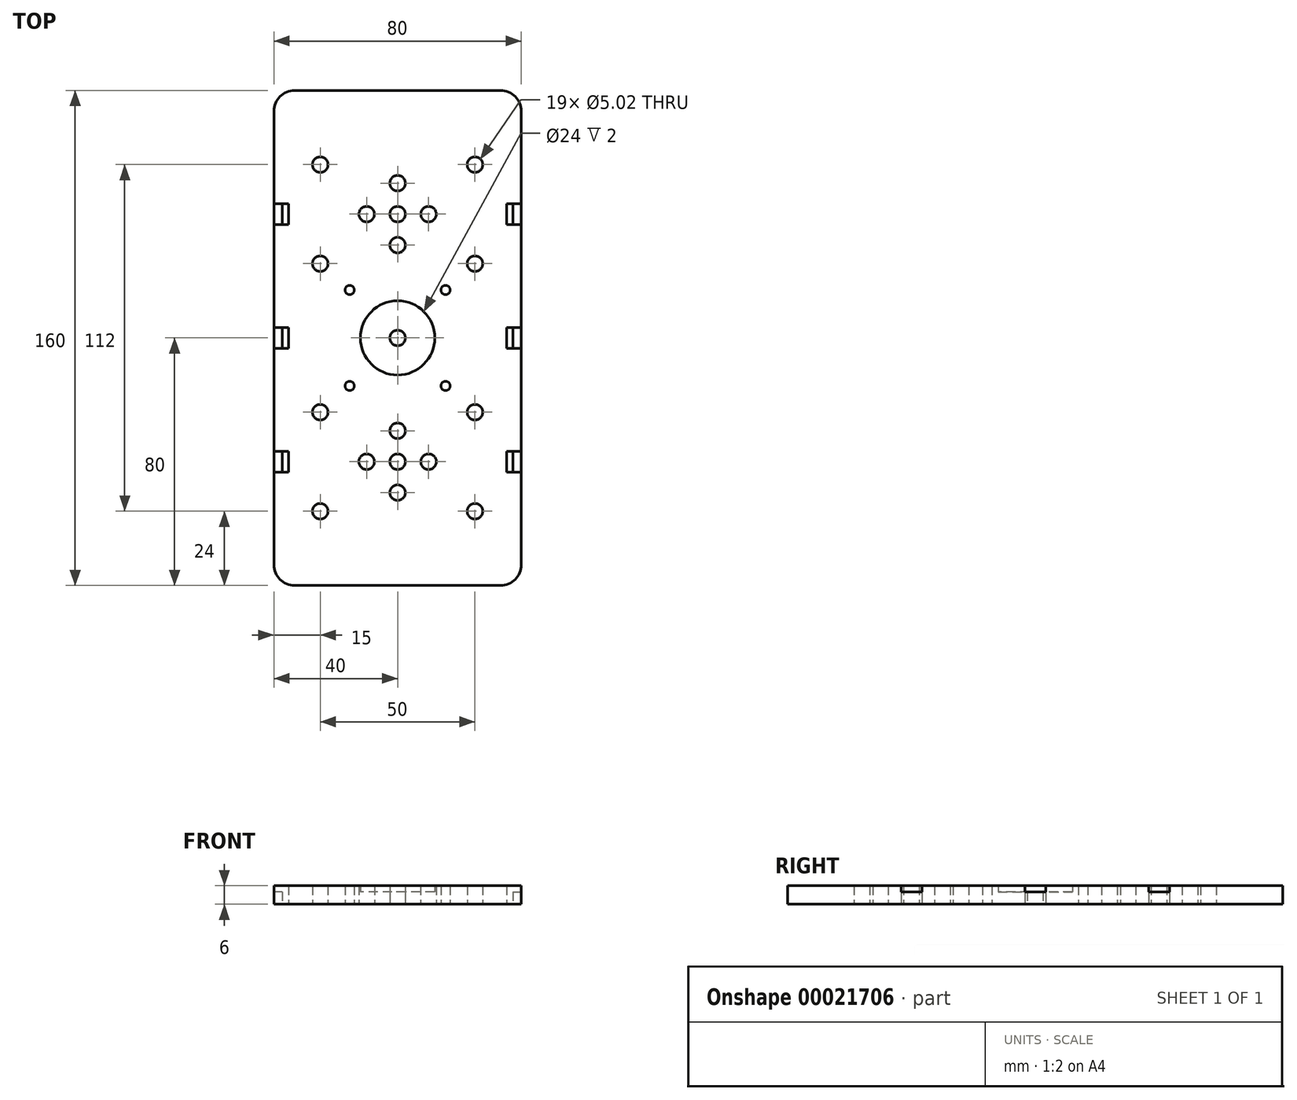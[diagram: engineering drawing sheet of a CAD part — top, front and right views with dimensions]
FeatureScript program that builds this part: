
annotation { "Feature Type Name" : "Feature", "Feature Type Description" : "" }
export const myFeature = defineFeature(function(context is Context, id is Id, definition is map)
    precondition{}
    {
        {
            var Q0;
            Q0=qCreatedBy(makeId("Top.planeOp"),FACE);
            var sketch = newSketch(context, id + "F2", { "sketchPlane" : qUnion([Q0])});
            skLineSegment(sketch, "E0", {"start": v(0, 0) * mm, "end": v(0, 40) * mm, "construction": true});
            skLineSegment(sketch, "E1", {"start": v(0, 0) * mm, "end": v(40, 0) * mm, "construction": true});
            skLineSegment(sketch, "E2", {"start": v(40, 0) * mm, "end": v(40, 33.3) * mm});
            skLineSegment(sketch, "E3", {"start": v(33.3, 40) * mm, "end": v(0, 40) * mm});
            skCircle(sketch, "E4", {"center": v(0, 0) * mm, "radius": 2.5 * mm, "construction": true});
            skLineSegment(sketch, "E5", {"start": v(25, 0) * mm, "end": v(25, 16) * mm, "construction": true});
            skLineSegment(sketch, "E6", {"start": v(25, 16) * mm, "end": v(0, 16) * mm, "construction": true});
            skCircle(sketch, "E7", {"center": v(25, 16) * mm, "radius": 2.5 * mm});
            skPoint(sketch, "E8.visualSharp", {"position": v(40, 40) * mm});
            skArc(sketch, "E8.filletArc", {"start": v(40, 33.3) * mm, "mid": v(38.04, 38.04) * mm, "end": v(33.3, 40) * mm});
            skLineSegment(sketch, "E9", {"start": v(37.26, 0) * mm, "end": v(37.26, 3.35) * mm});
            skLineSegment(sketch, "E10", {"start": v(37.26, 3.35) * mm, "end": v(40, 3.35) * mm});
            skLineSegment(sketch, "E11", {"start": v(37.26, 3.35) * mm, "end": v(35.26, 3.35) * mm});
            skLineSegment(sketch, "E12", {"start": v(35.26, 3.35) * mm, "end": v(35.26, 0) * mm});
            skCircle(sketch, "E13", {"center": v(10, 0) * mm, "radius": 2.5 * mm, "construction": true});
            skCircle(sketch, "E14", {"center": v(0, 10) * mm, "radius": 2.5 * mm, "construction": true});
            skLineSegment(sketch, "E15", {"start": v(10, 0) * mm, "end": v(0, 0) * mm, "construction": true});
            skLineSegment(sketch, "E16", {"start": v(0, 10) * mm, "end": v(0, 0) * mm, "construction": true});
            skArc(sketch, "E17", {"start": v(2.5, 0) * mm, "mid": v(1.77, 1.77) * mm, "end": v(0, 2.5) * mm});
            skArc(sketch, "E18", {"start": v(12.5, 0) * mm, "mid": v(10, 2.51) * mm, "end": v(7.5, 0) * mm});
            skArc(sketch, "E19", {"start": v(0, 7.5) * mm, "mid": v(2.5, 10) * mm, "end": v(0, 12.5) * mm});
            skArc(sketch, "E20.MirrorCS", {"start": v(0, 7.5) * mm, "mid": v(-2.5, 10) * mm, "end": v(0, 12.5) * mm});
            skArc(sketch, "E21.MirrorCS", {"start": v(-2.5, 0) * mm, "mid": v(-1.77, 1.77) * mm, "end": v(0, 2.5) * mm});
            skArc(sketch, "E22.MirrorCS", {"start": v(-12.5, 0) * mm, "mid": v(-10, 2.51) * mm, "end": v(-7.5, 0) * mm});
            skLineSegment(sketch, "E23.MirrorCS", {"start": v(-33.3, 40) * mm, "end": v(0, 40) * mm});
            skArc(sketch, "E24.MirrorCS", {"start": v(-40, 33.3) * mm, "mid": v(-38.04, 38.04) * mm, "end": v(-33.3, 40) * mm});
            skLineSegment(sketch, "E25.MirrorCS", {"start": v(-40, 0) * mm, "end": v(-40, 33.3) * mm});
            skLineSegment(sketch, "E26.MirrorCS", {"start": v(-37.26, 3.35) * mm, "end": v(-40, 3.35) * mm});
            skLineSegment(sketch, "E27.MirrorCS", {"start": v(-37.26, 0) * mm, "end": v(-37.26, 3.35) * mm});
            skLineSegment(sketch, "E28.MirrorCS", {"start": v(-37.26, 3.35) * mm, "end": v(-35.26, 3.35) * mm});
            skLineSegment(sketch, "E29.MirrorCS", {"start": v(-35.26, 3.35) * mm, "end": v(-35.26, 0) * mm});
            skCircle(sketch, "E30.MirrorC", {"center": v(-25, 16) * mm, "radius": 2.5 * mm});
            skLineSegment(sketch, "E31.MirrorCS", {"start": v(-40, 0) * mm, "end": v(-40, -40) * mm});
            skLineSegment(sketch, "E32.MirrorCS", {"start": v(-37.26, -3.35) * mm, "end": v(-40, -3.35) * mm});
            skLineSegment(sketch, "E33.MirrorCS", {"start": v(-37.26, 0) * mm, "end": v(-37.26, -3.35) * mm});
            skLineSegment(sketch, "E34.MirrorCS", {"start": v(-35.26, -3.35) * mm, "end": v(-35.26, 0) * mm});
            skLineSegment(sketch, "E35.MirrorCS", {"start": v(-37.26, -3.35) * mm, "end": v(-35.26, -3.35) * mm});
            skArc(sketch, "E36.MirrorCS", {"start": v(-12.5, 0) * mm, "mid": v(-10, -2.51) * mm, "end": v(-7.5, 0) * mm});
            skCircle(sketch, "E37.MirrorC", {"center": v(-25, -16) * mm, "radius": 2.5 * mm});
            skLineSegment(sketch, "E38.MirrorCS", {"start": v(-40, -40) * mm, "end": v(0, -40) * mm, "construction": true});
            skArc(sketch, "E39.MirrorCS", {"start": v(-2.5, 0) * mm, "mid": v(-1.77, -1.77) * mm, "end": v(0, -2.5) * mm});
            skArc(sketch, "E40.MirrorCS", {"start": v(2.5, 0) * mm, "mid": v(1.77, -1.77) * mm, "end": v(0, -2.5) * mm});
            skArc(sketch, "E41.MirrorCS", {"start": v(0, -7.5) * mm, "mid": v(2.5, -10) * mm, "end": v(0, -12.5) * mm});
            skArc(sketch, "E42.MirrorCS", {"start": v(0, -7.5) * mm, "mid": v(-2.5, -10) * mm, "end": v(0, -12.5) * mm});
            skArc(sketch, "E43.MirrorCS", {"start": v(12.5, 0) * mm, "mid": v(10, -2.51) * mm, "end": v(7.5, 0) * mm});
            skCircle(sketch, "E44.MirrorC", {"center": v(25, -16) * mm, "radius": 2.5 * mm});
            skLineSegment(sketch, "E45.MirrorCS", {"start": v(40, -40) * mm, "end": v(0, -40) * mm, "construction": true});
            skLineSegment(sketch, "E46.MirrorCS", {"start": v(40, 0) * mm, "end": v(40, -40) * mm});
            skLineSegment(sketch, "E47.MirrorCS", {"start": v(35.26, -3.35) * mm, "end": v(35.26, 0) * mm});
            skLineSegment(sketch, "E48.MirrorCS", {"start": v(37.26, -3.35) * mm, "end": v(35.26, -3.35) * mm});
            skLineSegment(sketch, "E49.MirrorCS", {"start": v(37.26, 0) * mm, "end": v(37.26, -3.35) * mm});
            skLineSegment(sketch, "E50.MirrorCS", {"start": v(37.26, -3.35) * mm, "end": v(40, -3.35) * mm});
            skPoint(sketch, "E51.orphan", {"position": v(-40, -33.3) * mm});
            skPoint(sketch, "E52.orphan", {"position": v(40, -33.3) * mm});
            skPoint(sketch, "E53.orphan", {"position": v(-33.3, -40) * mm});
            skPoint(sketch, "E54.orphan", {"position": v(33.3, -40) * mm});
            skLineSegment(sketch, "E55.MirrorCS", {"start": v(-37.26, -76.65) * mm, "end": v(-35.26, -76.65) * mm});
            skLineSegment(sketch, "E56.MirrorCS", {"start": v(37.26, -83.35) * mm, "end": v(35.26, -83.35) * mm});
            skLineSegment(sketch, "E57.MirrorCS", {"start": v(37.26, -76.65) * mm, "end": v(35.26, -76.65) * mm});
            skLineSegment(sketch, "E58.MirrorCS", {"start": v(37.26, -80) * mm, "end": v(37.26, -83.35) * mm});
            skLineSegment(sketch, "E59.MirrorCS", {"start": v(-35.25, -76.65) * mm, "end": v(-35.25, -80) * mm});
            skLineSegment(sketch, "E60.MirrorCS", {"start": v(35.26, -83.35) * mm, "end": v(35.26, -80) * mm});
            skLineSegment(sketch, "E61.MirrorCS", {"start": v(-37.26, -80) * mm, "end": v(-37.25, -83.35) * mm});
            skLineSegment(sketch, "E62.MirrorCS", {"start": v(-35.25, -83.35) * mm, "end": v(-35.25, -80) * mm});
            skLineSegment(sketch, "E63.MirrorCS", {"start": v(-37.26, -83.35) * mm, "end": v(-35.26, -83.35) * mm});
            skArc(sketch, "E64.MirrorCS", {"start": v(2.5, -80) * mm, "mid": v(1.77, -78.23) * mm, "end": v(0, -77.49) * mm});
            skLineSegment(sketch, "E65.MirrorCS", {"start": v(37.26, -80) * mm, "end": v(37.26, -76.65) * mm});
            skLineSegment(sketch, "E66.MirrorCS", {"start": v(-37.25, -80) * mm, "end": v(-37.25, -76.65) * mm});
            skLineSegment(sketch, "E67.MirrorCS", {"start": v(35.26, -76.65) * mm, "end": v(35.26, -80) * mm});
            skCircle(sketch, "E68.MirrorC", {"center": v(10, -80) * mm, "radius": 2.5 * mm});
            skCircle(sketch, "E69.MirrorC", {"center": v(0, -90) * mm, "radius": 2.5 * mm});
            skLineSegment(sketch, "E70.MirrorCS", {"start": v(10, -80) * mm, "end": v(0, -80) * mm, "construction": true});
            skCircle(sketch, "E71.MirrorC", {"center": v(0, -80) * mm, "radius": 2.5 * mm});
            skLineSegment(sketch, "E72.MirrorCS", {"start": v(37.26, -83.35) * mm, "end": v(40, -83.35) * mm});
            skLineSegment(sketch, "E73.MirrorCS", {"start": v(37.26, -76.65) * mm, "end": v(40, -76.65) * mm});
            skArc(sketch, "E74.MirrorCS", {"start": v(-2.5, -80) * mm, "mid": v(-1.77, -78.23) * mm, "end": v(0, -77.49) * mm});
            skLineSegment(sketch, "E75.MirrorCS", {"start": v(-37.26, -83.35) * mm, "end": v(-40, -83.35) * mm});
            skLineSegment(sketch, "E76.MirrorCS", {"start": v(-37.26, -76.65) * mm, "end": v(-40, -76.65) * mm});
            skArc(sketch, "E77.MirrorCS", {"start": v(0, -72.5) * mm, "mid": v(-2.5, -70) * mm, "end": v(0, -67.49) * mm});
            skArc(sketch, "E78.MirrorCS", {"start": v(0, -87.49) * mm, "mid": v(2.5, -90) * mm, "end": v(0, -92.5) * mm});
            skPoint(sketch, "E79.MirrorP", {"position": v(40, -120) * mm});
            skLineSegment(sketch, "E80.MirrorCS", {"start": v(0, -80) * mm, "end": v(0, -120) * mm, "construction": true});
            skLineSegment(sketch, "E81.MirrorCS", {"start": v(0, -80) * mm, "end": v(40, -80) * mm, "construction": true});
            skLineSegment(sketch, "E82.MirrorCS", {"start": v(40, -80) * mm, "end": v(40, -113.3) * mm});
            skLineSegment(sketch, "E83.MirrorCS", {"start": v(33.3, -120) * mm, "end": v(0, -120) * mm});
            skLineSegment(sketch, "E84.MirrorCS", {"start": v(25, -80) * mm, "end": v(25, -96) * mm, "construction": true});
            skLineSegment(sketch, "E85.MirrorCS", {"start": v(25, -96) * mm, "end": v(0, -96) * mm, "construction": true});
            skCircle(sketch, "E86.MirrorC", {"center": v(25, -96) * mm, "radius": 2.5 * mm});
            skArc(sketch, "E87.MirrorCS", {"start": v(40, -113.3) * mm, "mid": v(38.04, -118.04) * mm, "end": v(33.3, -120) * mm});
            skArc(sketch, "E88.MirrorCS", {"start": v(12.5, -80) * mm, "mid": v(10, -77.49) * mm, "end": v(7.5, -80) * mm});
            skLineSegment(sketch, "E89.MirrorCS", {"start": v(-33.3, -120) * mm, "end": v(0, -120) * mm});
            skArc(sketch, "E90.MirrorCS", {"start": v(0, -87.49) * mm, "mid": v(-2.5, -90) * mm, "end": v(0, -92.5) * mm});
            skArc(sketch, "E91.MirrorCS", {"start": v(-12.5, -80) * mm, "mid": v(-10, -77.49) * mm, "end": v(-7.5, -80) * mm});
            skLineSegment(sketch, "E92.MirrorCS", {"start": v(0, -90) * mm, "end": v(0, -80) * mm, "construction": true});
            skPoint(sketch, "E93.MirrorP", {"position": v(-40, -46.7) * mm});
            skCircle(sketch, "E94.MirrorC", {"center": v(25, -64) * mm, "radius": 2.5 * mm});
            skArc(sketch, "E95.MirrorCS", {"start": v(-40, -113.3) * mm, "mid": v(-38.04, -118.04) * mm, "end": v(-33.3, -120) * mm});
            skArc(sketch, "E96.MirrorCS", {"start": v(-2.5, -80) * mm, "mid": v(-1.77, -81.77) * mm, "end": v(0, -82.5) * mm});
            skCircle(sketch, "E97.MirrorC", {"center": v(-25, -64) * mm, "radius": 2.5 * mm});
            skCircle(sketch, "E98.MirrorC", {"center": v(-25, -96) * mm, "radius": 2.5 * mm});
            skLineSegment(sketch, "E99.MirrorCS", {"start": v(40, -80) * mm, "end": v(40, -40) * mm});
            skArc(sketch, "E100.MirrorCS", {"start": v(2.5, -80) * mm, "mid": v(1.77, -81.77) * mm, "end": v(0, -82.5) * mm});
            skPoint(sketch, "E101.MirrorP", {"position": v(40, -46.7) * mm});
            skArc(sketch, "E102.MirrorCS", {"start": v(0, -72.5) * mm, "mid": v(2.5, -70) * mm, "end": v(0, -67.49) * mm});
            skLineSegment(sketch, "E103.MirrorCS", {"start": v(-40, -80) * mm, "end": v(-40, -113.3) * mm});
            skArc(sketch, "E104.MirrorCS", {"start": v(-12.5, -80) * mm, "mid": v(-10, -82.5) * mm, "end": v(-7.5, -80) * mm});
            skLineSegment(sketch, "E105.MirrorCS", {"start": v(-40, -80) * mm, "end": v(-40, -40) * mm});
            skArc(sketch, "E106.MirrorCS", {"start": v(12.5, -80) * mm, "mid": v(10, -82.5) * mm, "end": v(7.5, -80) * mm});
            skLineSegment(sketch, "E107", {"start": v(37.26, -40) * mm, "end": v(37.26, -36.65) * mm});
            skLineSegment(sketch, "E108", {"start": v(37.26, -36.65) * mm, "end": v(40, -36.65) * mm});
            skLineSegment(sketch, "E109", {"start": v(37.26, -36.65) * mm, "end": v(35.26, -36.65) * mm});
            skLineSegment(sketch, "E110", {"start": v(35.26, -36.65) * mm, "end": v(35.26, -40) * mm});
            skLineSegment(sketch, "E111.MirrorCS", {"start": v(37.26, -43.35) * mm, "end": v(40, -43.35) * mm});
            skLineSegment(sketch, "E112.MirrorCS", {"start": v(37.26, -43.35) * mm, "end": v(35.26, -43.35) * mm});
            skLineSegment(sketch, "E113.MirrorCS", {"start": v(35.26, -43.35) * mm, "end": v(35.26, -40) * mm});
            skLineSegment(sketch, "E114.MirrorCS", {"start": v(37.26, -40) * mm, "end": v(37.26, -43.35) * mm});
            skLineSegment(sketch, "E115.MirrorCS", {"start": v(-35.25, -36.65) * mm, "end": v(-35.25, -40) * mm});
            skLineSegment(sketch, "E116.MirrorCS", {"start": v(-37.25, -36.65) * mm, "end": v(-35.25, -36.65) * mm});
            skLineSegment(sketch, "E117.MirrorCS", {"start": v(-37.25, -40) * mm, "end": v(-37.25, -36.65) * mm});
            skLineSegment(sketch, "E118.MirrorCS", {"start": v(-37.25, -36.65) * mm, "end": v(-40, -36.65) * mm});
            skLineSegment(sketch, "E119.MirrorCS", {"start": v(-37.25, -43.35) * mm, "end": v(-40, -43.35) * mm});
            skLineSegment(sketch, "E120.MirrorCS", {"start": v(-37.25, -43.35) * mm, "end": v(-35.25, -43.35) * mm});
            skLineSegment(sketch, "E121.MirrorCS", {"start": v(-35.25, -43.35) * mm, "end": v(-35.25, -40) * mm});
            skLineSegment(sketch, "E122.MirrorCS", {"start": v(-37.25, -40) * mm, "end": v(-37.25, -43.35) * mm});
            skCircle(sketch, "E123", {"center": v(0, -40) * mm, "radius": 2.51 * mm});
            skCircle(sketch, "E124", {"center": v(0, -40) * mm, "radius": 12 * mm});
            skLineSegment(sketch, "E125", {"start": v(0, -40) * mm, "end": v(0, -24.5) * mm, "construction": true});
            skLineSegment(sketch, "E126", {"start": v(0, -24.5) * mm, "end": v(-15.5, -24.5) * mm, "construction": true});
            skCircle(sketch, "E127", {"center": v(-15.5, -24.5) * mm, "radius": 1.5 * mm});
            skCircle(sketch, "E128.MirrorC", {"center": v(-15.5, -55.5) * mm, "radius": 1.5 * mm});
            skCircle(sketch, "E129.MirrorC", {"center": v(15.5, -24.5) * mm, "radius": 1.5 * mm});
            skCircle(sketch, "E130.MirrorC", {"center": v(15.5, -55.5) * mm, "radius": 1.5 * mm});
            skLineSegment(sketch, "E131", {"start": v(0, -80) * mm, "end": v(0, 0) * mm, "construction": true});
            skSolve(sketch);
        }
        {
            var Q0;
            Q0=makeQuery(id+"F2.imprint","IMPRINT",FACE,{"disambiguationData":[TD([[makeQuery(id+"F2.imprint","IMPRINT",EDGE,{"derivedFrom":sQuery(id+"F2.wireOp",EDGE,"E3")}),1.0]])]});
            extrude(context, id + "F0", {"entities" : qUnion([Q0]), "depth" : 6 * mm});
        }
        {
            var Q0;
            {var subQ4=sQuery(id+"F2.wireOp",EDGE,"E26.MirrorCS");Q0=makeQuery(id+"F2.imprint","IMPRINT",FACE,{"disambiguationData":[TD([[makeQuery(id+"F2.imprint","IMPRINT",EDGE,{"derivedFrom":subQ4}),1.0]])]});}
            var Q1;
            Q1=makeQuery(id+"F2.imprint","IMPRINT",FACE,{"disambiguationData":[TD([[makeQuery(id+"F2.imprint","IMPRINT",EDGE,{"derivedFrom":sQuery(id+"F2.wireOp",EDGE,"E9")}),-1.0]])]});
            var Q2;
            Q2=makeQuery(id+"F2.imprint","IMPRINT",FACE,{"disambiguationData":[TD([[makeQuery(id+"F2.imprint","IMPRINT",EDGE,{"derivedFrom":sQuery(id+"F2.wireOp",EDGE,"E61.MirrorCS")}),-1.0]])]});
            var Q3;
            Q3=makeQuery(id+"F2.imprint","IMPRINT",FACE,{"disambiguationData":[TD([[makeQuery(id+"F2.imprint","IMPRINT",EDGE,{"derivedFrom":sQuery(id+"F2.wireOp",EDGE,"E58.MirrorCS")}),1.0]])]});
            var Q4;
            Q4=makeQuery(id+"F2.imprint","IMPRINT",FACE,{"disambiguationData":[TD([[makeQuery(id+"F2.imprint","IMPRINT",EDGE,{"derivedFrom":sQuery(id+"F2.wireOp",EDGE,"E117.MirrorCS")}),1.0]])]});
            var Q5;
            Q5=makeQuery(id+"F2.imprint","IMPRINT",FACE,{"disambiguationData":[TD([[makeQuery(id+"F2.imprint","IMPRINT",EDGE,{"derivedFrom":sQuery(id+"F2.wireOp",EDGE,"E107")}),-1.0]])]});
            extrude(context, id + "F3", {"entities" : qUnion([Q0, Q1, Q2, Q3, Q4, Q5]), "operationType" : NewBodyOperationType.ADD, "depth" : 4 * mm});
        }
        {
            var Q0;
            Q0=makeQuery(id+"F2.imprint","IMPRINT",FACE,{"disambiguationData":[TD([[makeQuery(id+"F2.imprint","IMPRINT",EDGE,{"derivedFrom":sQuery(id+"F2.wireOp",EDGE,"E123")}),-1.0]])]});
            extrude(context, id + "F1", {"entities" : qUnion([Q0]), "operationType" : NewBodyOperationType.ADD, "depth" : 4 * mm});
        }
    });
